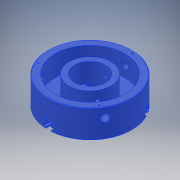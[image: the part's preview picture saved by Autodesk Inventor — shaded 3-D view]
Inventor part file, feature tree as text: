
AUTODESK INVENTOR PART (.ipt)
format: ipt  version: 2018 (Build 220112000, 112)  size: 281,600 bytes
history: native  units: in
note: dims shown in document units (in); Inventor stores cm internally (conversion verified against a paired STEP export)
features: extrude x4, sketch x3, plane x2, revolve x1, other x1, pattern_circular x1, chamfer x1, projected_geometry x1, reference x1
ambient origin geometry x8: Origin, YZ Plane, XZ Plane, XY Plane, X Axis, Y Axis, Z Axis, Center Point
bodies: Solid1 (feature_tree)
feature tree (15):
  revolve  "Revolution3"  [1 undecoded]
  extrude  "Extrusion8"  Depth=0.1969in
  plane  "Work Plane1"
  extrude  "Extrusion12"  Depth=1.1811in
  extrude  "Extrusion13"  TaperAngle=90.0deg  [1 undecoded]
  plane  "Work Plane2"
  other  "Work Axis2"
  extrude  "Extrusion14"  Depth=1.1811in
  pattern_circular  "Circular Pattern1"  [2 undecoded]
  chamfer  "Chamfer1"  Distance=0.1378in
  projected_geometry  "Projected Loop1"
  sketch  "Sketch15"  dims[d51=0.5906in d52=0.1575in]
  reference  "Reference2"
  sketch  "Sketch16"  dims[d53=0.9843in d54=0.1969in]
  sketch  "Sketch17"  dims[d55=0.1969in d56=0.5906in d58=90.0deg d60=0.0787in d61=0.0787in d62=0.1378in d63=0.0787in d64=0.0394in d65=0.3937in d66=0.0in d67=0.0in d68=0.0787in d69=0.0in d72=-1.378in d78=0.3937in d79=0.0in d80=0.3937in d81=0.0in d82=-1.1811in d83=0.1969in d84=0.3937in d85=0.0in d86=0.0394in d87=1.1811in d88=360.0deg d90=0.0157in d91=0.0787in d92=45.0deg]
note: 4 required parameter values undecoded (feature->parameter linkage not recoverable at this tier; creation-order binding heuristic only, values carry confidence <= 0.55)